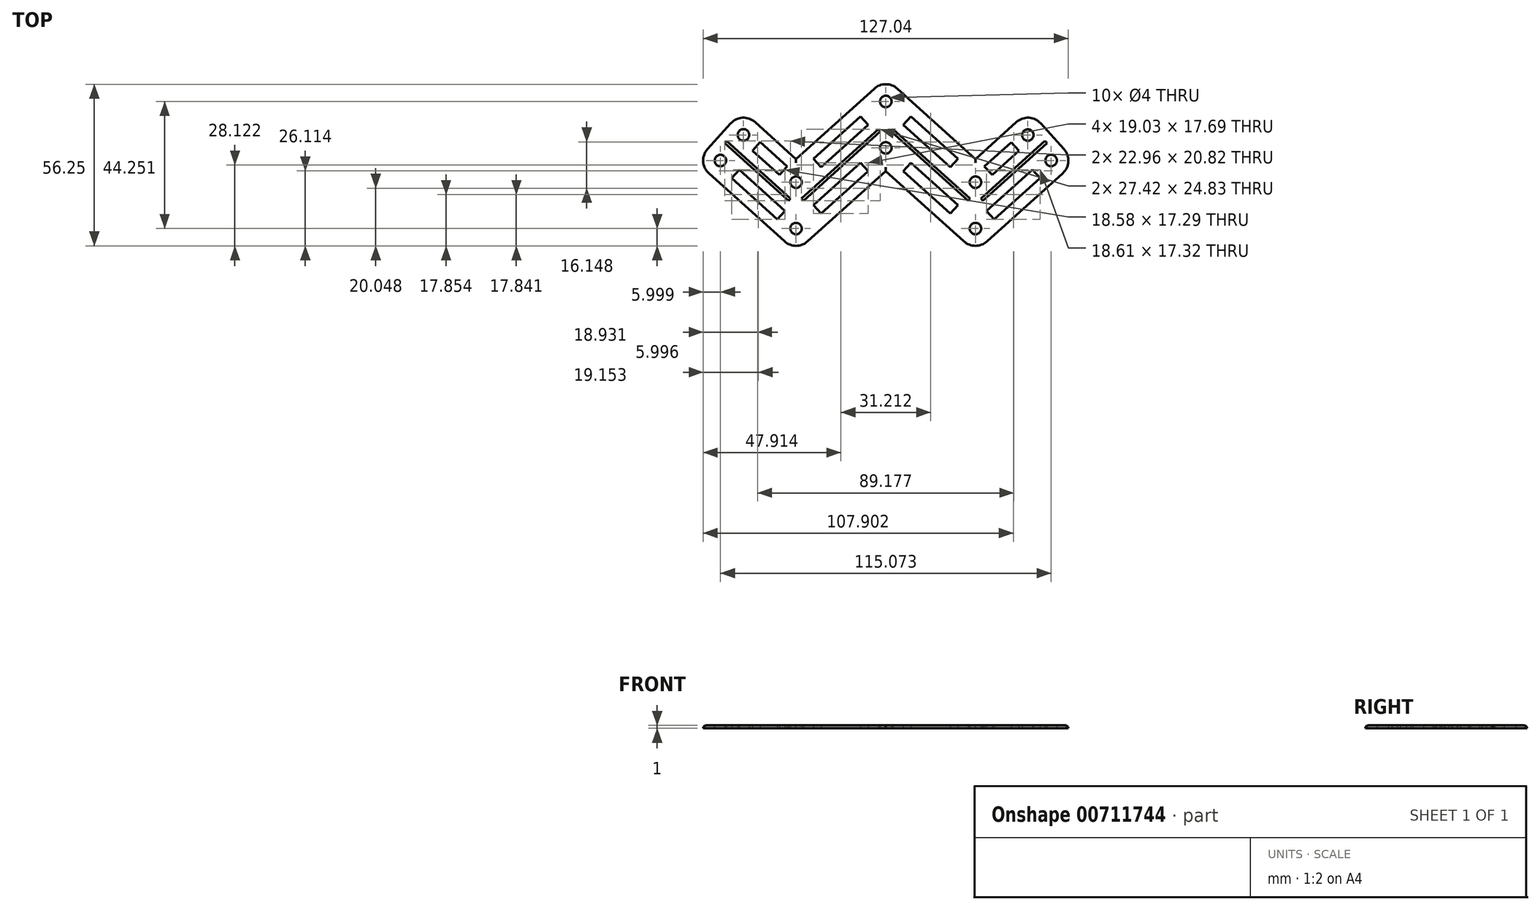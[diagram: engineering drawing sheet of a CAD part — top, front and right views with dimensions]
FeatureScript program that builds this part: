
annotation { "Feature Type Name" : "Feature", "Feature Type Description" : "" }
export const myFeature = defineFeature(function(context is Context, id is Id, definition is map)
    precondition{}
    {
        {
            var Q0;
            Q0=qCreatedBy(makeId("Top.planeOp"),FACE);
            var sketch = newSketch(context, id + "F0", { "sketchPlane" : qUnion([Q0])});
            skLineSegment(sketch, "E0", {"start": v(-57.97, 24.09) * mm, "end": v(-31.21, 0) * mm});
            skLineSegment(sketch, "E1", {"start": v(-31.21, 0) * mm, "end": v(0, 28.1) * mm});
            skLineSegment(sketch, "E2", {"start": v(0, 28.1) * mm, "end": v(31.21, 0) * mm});
            skLineSegment(sketch, "E3", {"start": v(31.21, 0) * mm, "end": v(57.97, 24.09) * mm});
            skLineSegment(sketch, "E4.0", {"start": v(31.21, -0.67) * mm, "end": v(58.3, 23.72) * mm});
            skLineSegment(sketch, "E4.1", {"start": v(0, 27.43) * mm, "end": v(31.21, -0.67) * mm});
            skLineSegment(sketch, "E4.2", {"start": v(-31.21, -0.67) * mm, "end": v(0, 27.43) * mm});
            skLineSegment(sketch, "E4.3", {"start": v(-58.3, 23.72) * mm, "end": v(-31.21, -0.67) * mm});
            skLineSegment(sketch, "E5.0", {"start": v(31.21, 0.67) * mm, "end": v(57.63, 24.46) * mm});
            skLineSegment(sketch, "E5.1", {"start": v(0, 28.78) * mm, "end": v(31.21, 0.67) * mm});
            skLineSegment(sketch, "E5.2", {"start": v(-31.21, 0.67) * mm, "end": v(0, 28.78) * mm});
            skLineSegment(sketch, "E5.3", {"start": v(-57.63, 24.46) * mm, "end": v(-31.21, 0.67) * mm});
            skLineSegment(sketch, "E6", {"start": v(-58.3, 23.72) * mm, "end": v(-57.97, 24.09) * mm});
            skLineSegment(sketch, "E7", {"start": v(-57.97, 24.09) * mm, "end": v(-57.63, 24.46) * mm});
            skLineSegment(sketch, "E8", {"start": v(57.63, 24.46) * mm, "end": v(57.97, 24.09) * mm});
            skLineSegment(sketch, "E9", {"start": v(58.3, 23.72) * mm, "end": v(57.97, 24.09) * mm});
            skLineSegment(sketch, "E10.0", {"start": v(35.23, -12.53) * mm, "end": v(61.54, 11.16) * mm});
            skLineSegment(sketch, "E10.1", {"start": v(0, 11.96) * mm, "end": v(27.2, -12.53) * mm});
            skLineSegment(sketch, "E10.2", {"start": v(-27.2, -12.53) * mm, "end": v(0, 11.96) * mm});
            skLineSegment(sketch, "E10.3", {"start": v(-61.54, 11.16) * mm, "end": v(-35.23, -12.53) * mm});
            skLineSegment(sketch, "E11.0", {"start": v(31.21, 16.15) * mm, "end": v(45.48, 29) * mm});
            skLineSegment(sketch, "E11.1", {"start": v(4.01, 40.64) * mm, "end": v(31.21, 16.15) * mm});
            skLineSegment(sketch, "E11.2", {"start": v(-31.21, 16.15) * mm, "end": v(-4.01, 40.64) * mm});
            skLineSegment(sketch, "E11.3", {"start": v(-45.48, 29) * mm, "end": v(-31.21, 16.15) * mm});
            skLineSegment(sketch, "E12", {"start": v(-61.98, 19.63) * mm, "end": v(-58.3, 23.72) * mm});
            skLineSegment(sketch, "E13", {"start": v(-53.95, 28.55) * mm, "end": v(-57.63, 24.46) * mm});
            skLineSegment(sketch, "E14", {"start": v(61.98, 19.63) * mm, "end": v(58.3, 23.72) * mm});
            skLineSegment(sketch, "E15", {"start": v(53.95, 28.55) * mm, "end": v(57.63, 24.46) * mm});
            skLineSegment(sketch, "E16.0", {"start": v(31.21, -8.07) * mm, "end": v(62.01, 19.66) * mm, "construction": true});
            skLineSegment(sketch, "E16.1", {"start": v(0, 20.03) * mm, "end": v(31.21, -8.07) * mm, "construction": true});
            skLineSegment(sketch, "E16.2", {"start": v(-31.21, -8.07) * mm, "end": v(0, 20.03) * mm, "construction": true});
            skLineSegment(sketch, "E16.3", {"start": v(-61.98, 19.63) * mm, "end": v(-31.21, -8.07) * mm, "construction": true});
            skLineSegment(sketch, "E17.0", {"start": v(31.21, 8.07) * mm, "end": v(53.9, 28.5) * mm, "construction": true});
            skLineSegment(sketch, "E17.1", {"start": v(0, 36.18) * mm, "end": v(31.21, 8.07) * mm, "construction": true});
            skLineSegment(sketch, "E17.2", {"start": v(-31.21, 8.07) * mm, "end": v(0, 36.18) * mm, "construction": true});
            skLineSegment(sketch, "E17.3", {"start": v(-53.95, 28.55) * mm, "end": v(-31.21, 8.07) * mm, "construction": true});
            skCircle(sketch, "E18", {"center": v(-31.21, 8.07) * mm, "radius": 2 * mm});
            skCircle(sketch, "E19", {"center": v(-31.21, -8.07) * mm, "radius": 2 * mm});
            skCircle(sketch, "E20", {"center": v(0, 20.03) * mm, "radius": 2 * mm});
            skCircle(sketch, "E21", {"center": v(0, 36.18) * mm, "radius": 2 * mm});
            skCircle(sketch, "E22", {"center": v(31.21, 8.07) * mm, "radius": 2 * mm});
            skCircle(sketch, "E23", {"center": v(31.21, -8.07) * mm, "radius": 2 * mm});
            skCircle(sketch, "E24", {"center": v(49.43, 24.48) * mm, "radius": 2 * mm});
            skCircle(sketch, "E25", {"center": v(57.55, 15.64) * mm, "radius": 2 * mm});
            skCircle(sketch, "E26", {"center": v(-57.52, 15.62) * mm, "radius": 2 * mm});
            skCircle(sketch, "E27", {"center": v(-49.5, 24.53) * mm, "radius": 2 * mm});
            skLineSegment(sketch, "E28.0", {"start": v(31.21, -10.77) * mm, "end": v(63.32, 18.14) * mm, "construction": true});
            skLineSegment(sketch, "E28.1", {"start": v(0, 17.34) * mm, "end": v(31.21, -10.77) * mm, "construction": true});
            skLineSegment(sketch, "E28.2", {"start": v(-31.21, -10.77) * mm, "end": v(0, 17.34) * mm, "construction": true});
            skLineSegment(sketch, "E28.3", {"start": v(-63.32, 18.14) * mm, "end": v(-31.21, -10.77) * mm, "construction": true});
            skLineSegment(sketch, "E29.0", {"start": v(31.21, -5.38) * mm, "end": v(60.64, 21.12) * mm, "construction": true});
            skLineSegment(sketch, "E29.1", {"start": v(4.01, 19.1) * mm, "end": v(31.21, -5.38) * mm, "construction": true});
            skLineSegment(sketch, "E29.2", {"start": v(-31.21, -5.38) * mm, "end": v(-4.01, 19.1) * mm, "construction": true});
            skLineSegment(sketch, "E29.3", {"start": v(-60.64, 21.12) * mm, "end": v(-31.21, -5.38) * mm, "construction": true});
            skLineSegment(sketch, "E30.0", {"start": v(31.21, 10.77) * mm, "end": v(52.61, 30.03) * mm, "construction": true});
            skLineSegment(sketch, "E30.1", {"start": v(0, 38.87) * mm, "end": v(31.21, 10.77) * mm, "construction": true});
            skLineSegment(sketch, "E30.2", {"start": v(-31.21, 10.77) * mm, "end": v(0, 38.87) * mm, "construction": true});
            skLineSegment(sketch, "E30.3", {"start": v(-52.61, 30.03) * mm, "end": v(-31.21, 10.77) * mm, "construction": true});
            skLineSegment(sketch, "E31.0", {"start": v(31.21, 5.38) * mm, "end": v(55.29, 27.06) * mm, "construction": true});
            skLineSegment(sketch, "E31.1", {"start": v(0, 33.49) * mm, "end": v(31.21, 5.38) * mm, "construction": true});
            skLineSegment(sketch, "E31.2", {"start": v(-31.21, 5.38) * mm, "end": v(0, 33.49) * mm, "construction": true});
            skLineSegment(sketch, "E31.3", {"start": v(-55.29, 27.06) * mm, "end": v(-31.21, 5.38) * mm, "construction": true});
            skLineSegment(sketch, "E32", {"start": v(-25.12, 16.25) * mm, "end": v(-8.77, 30.97) * mm});
            skLineSegment(sketch, "E33", {"start": v(-8.77, 30.97) * mm, "end": v(-6.1, 28) * mm});
            skLineSegment(sketch, "E34", {"start": v(-25.12, 16.25) * mm, "end": v(-22.44, 13.28) * mm});
            skLineSegment(sketch, "E35", {"start": v(-22.44, 13.28) * mm, "end": v(-6.1, 28) * mm});
            skLineSegment(sketch, "E36", {"start": v(-43.7, 22) * mm, "end": v(-46.37, 19.03) * mm});
            skLineSegment(sketch, "E37", {"start": v(-46.37, 19.03) * mm, "end": v(-37.03, 10.62) * mm});
            skLineSegment(sketch, "E38", {"start": v(-37.03, 10.62) * mm, "end": v(-34.31, 13.56) * mm});
            skLineSegment(sketch, "E39", {"start": v(-34.31, 13.56) * mm, "end": v(-43.7, 22) * mm});
            skLineSegment(sketch, "E40", {"start": v(-50.98, 12.42) * mm, "end": v(-53.66, 9.44) * mm});
            skLineSegment(sketch, "E41", {"start": v(-53.66, 9.44) * mm, "end": v(-37.75, -4.88) * mm});
            skLineSegment(sketch, "E42", {"start": v(-37.75, -4.88) * mm, "end": v(-35.08, -1.9) * mm});
            skLineSegment(sketch, "E43", {"start": v(-35.08, -1.9) * mm, "end": v(-50.98, 12.42) * mm});
            skLineSegment(sketch, "E44", {"start": v(-22.44, -2.87) * mm, "end": v(-25.12, 0.1) * mm});
            skLineSegment(sketch, "E45", {"start": v(-25.12, 0.1) * mm, "end": v(-8.77, 14.82) * mm});
            skLineSegment(sketch, "E46", {"start": v(-8.77, 14.82) * mm, "end": v(-6.1, 11.85) * mm});
            skLineSegment(sketch, "E47", {"start": v(-6.1, 11.85) * mm, "end": v(-22.44, -2.87) * mm});
            skLineSegment(sketch, "E48", {"start": v(8.77, 30.97) * mm, "end": v(6.1, 28) * mm});
            skLineSegment(sketch, "E49", {"start": v(6.1, 28) * mm, "end": v(22.44, 13.28) * mm});
            skLineSegment(sketch, "E50", {"start": v(22.44, 13.28) * mm, "end": v(25.12, 16.25) * mm});
            skLineSegment(sketch, "E51", {"start": v(25.12, 16.25) * mm, "end": v(8.77, 30.97) * mm});
            skLineSegment(sketch, "E52", {"start": v(6.1, 11.85) * mm, "end": v(8.77, 14.82) * mm});
            skLineSegment(sketch, "E53", {"start": v(8.77, 14.82) * mm, "end": v(25.12, 0.1) * mm});
            skLineSegment(sketch, "E54", {"start": v(25.12, 0.1) * mm, "end": v(22.44, -2.87) * mm});
            skLineSegment(sketch, "E55", {"start": v(22.44, -2.87) * mm, "end": v(6.1, 11.85) * mm});
            skLineSegment(sketch, "E56", {"start": v(34.33, 13.57) * mm, "end": v(37, 10.6) * mm});
            skLineSegment(sketch, "E57", {"start": v(37, 10.6) * mm, "end": v(46.31, 18.98) * mm});
            skLineSegment(sketch, "E58", {"start": v(46.31, 18.98) * mm, "end": v(43.64, 21.95) * mm});
            skLineSegment(sketch, "E59", {"start": v(43.64, 21.95) * mm, "end": v(34.33, 13.57) * mm});
            skLineSegment(sketch, "E60", {"start": v(35.08, -1.9) * mm, "end": v(37.75, -4.88) * mm});
            skLineSegment(sketch, "E61", {"start": v(37.75, -4.88) * mm, "end": v(53.69, 9.47) * mm});
            skLineSegment(sketch, "E62", {"start": v(53.69, 9.47) * mm, "end": v(51.01, 12.44) * mm});
            skLineSegment(sketch, "E63", {"start": v(51.01, 12.44) * mm, "end": v(35.08, -1.9) * mm});
            skPoint(sketch, "E64.visualSharp", {"position": v(-49.94, 33) * mm});
            skArc(sketch, "E64.filletArc", {"start": v(-45.48, 29) * mm, "mid": v(-49.8, 30.52) * mm, "end": v(-53.95, 28.55) * mm});
            skPoint(sketch, "E65.visualSharp", {"position": v(-66, 15.17) * mm});
            skArc(sketch, "E65.filletArc", {"start": v(-61.98, 19.63) * mm, "mid": v(-63.51, 15.3) * mm, "end": v(-61.54, 11.16) * mm});
            skPoint(sketch, "E66.visualSharp", {"position": v(-31.21, -16.15) * mm});
            skArc(sketch, "E66.filletArc", {"start": v(-35.23, -12.53) * mm, "mid": v(-31.21, -14.07) * mm, "end": v(-27.2, -12.53) * mm});
            skPoint(sketch, "E67.visualSharp", {"position": v(0, 22.72) * mm});
            skArc(sketch, "E67.filletArc", {"start": v(4.01, 19.1) * mm, "mid": v(0, 20.65) * mm, "end": v(-4.01, 19.1) * mm, "construction": true});
            skPoint(sketch, "E68.visualSharp", {"position": v(0, 44.25) * mm});
            skArc(sketch, "E68.filletArc", {"start": v(4.01, 40.64) * mm, "mid": v(0, 42.18) * mm, "end": v(-4.01, 40.64) * mm});
            skPoint(sketch, "E69.visualSharp", {"position": v(31.21, -16.15) * mm});
            skArc(sketch, "E69.filletArc", {"start": v(27.2, -12.53) * mm, "mid": v(31.21, -14.07) * mm, "end": v(35.23, -12.53) * mm});
            skPoint(sketch, "E70.visualSharp", {"position": v(66, 15.17) * mm});
            skArc(sketch, "E70.filletArc", {"start": v(61.54, 11.16) * mm, "mid": v(63.51, 15.3) * mm, "end": v(61.98, 19.63) * mm});
            skPoint(sketch, "E71.visualSharp", {"position": v(49.94, 33) * mm});
            skArc(sketch, "E71.filletArc", {"start": v(53.95, 28.55) * mm, "mid": v(49.8, 30.52) * mm, "end": v(45.48, 29) * mm});
            skLineSegment(sketch, "E72", {"start": v(33.78, 1.64) * mm, "end": v(33.1, 2.38) * mm});
            skLineSegment(sketch, "E73", {"start": v(33.1, 2.38) * mm, "end": v(55.4, 22.45) * mm});
            skLineSegment(sketch, "E74", {"start": v(55.4, 22.45) * mm, "end": v(56.07, 21.7) * mm});
            skLineSegment(sketch, "E75", {"start": v(56.07, 21.7) * mm, "end": v(33.78, 1.64) * mm});
            skLineSegment(sketch, "E76", {"start": v(28.65, 1.64) * mm, "end": v(29.32, 2.38) * mm});
            skLineSegment(sketch, "E77", {"start": v(29.32, 2.38) * mm, "end": v(2.56, 26.47) * mm});
            skLineSegment(sketch, "E78", {"start": v(2.56, 26.47) * mm, "end": v(1.9, 25.72) * mm});
            skLineSegment(sketch, "E79", {"start": v(1.9, 25.72) * mm, "end": v(28.65, 1.64) * mm});
            skLineSegment(sketch, "E80", {"start": v(-2.56, 26.47) * mm, "end": v(-1.9, 25.72) * mm});
            skLineSegment(sketch, "E81", {"start": v(-1.9, 25.72) * mm, "end": v(-28.65, 1.64) * mm});
            skLineSegment(sketch, "E82", {"start": v(-28.65, 1.64) * mm, "end": v(-29.32, 2.38) * mm});
            skLineSegment(sketch, "E83", {"start": v(-29.32, 2.38) * mm, "end": v(-2.56, 26.47) * mm});
            skLineSegment(sketch, "E84", {"start": v(-33.78, 1.64) * mm, "end": v(-33.1, 2.38) * mm});
            skLineSegment(sketch, "E85", {"start": v(-33.1, 2.38) * mm, "end": v(-55.4, 22.45) * mm});
            skLineSegment(sketch, "E86", {"start": v(-55.4, 22.45) * mm, "end": v(-56.07, 21.7) * mm});
            skLineSegment(sketch, "E87", {"start": v(-56.07, 21.7) * mm, "end": v(-33.78, 1.64) * mm});
            skSolve(sketch);
        }
        {
            var Q0;
            Q0=makeQuery(id+"F0.imprint","IMPRINT",FACE,{"disambiguationData":[TD([[makeQuery(id+"F0.imprint","IMPRINT",EDGE,{"derivedFrom":sQuery(id+"F0.wireOp",EDGE,"E10.0")}),1.0]])]});
            var Q1;
            {var subQ0=sQuery(id+"F0.wireOp",EDGE,"E6");Q1=makeQuery(id+"F0.imprint","IMPRINT",FACE,{"disambiguationData":[TD([[makeQuery(id+"F0.imprint","IMPRINT",EDGE,{"derivedFrom":subQ0}),-1.0]])]});}
            var Q2;
            {var subQ0=sQuery(id+"F0.wireOp",EDGE,"E7");Q2=makeQuery(id+"F0.imprint","IMPRINT",FACE,{"disambiguationData":[TD([[makeQuery(id+"F0.imprint","IMPRINT",EDGE,{"derivedFrom":subQ0}),-1.0]])]});}
            var Q3;
            Q3=makeQuery(id+"F0.imprint","IMPRINT",FACE,{"disambiguationData":[TD([[makeQuery(id+"F0.imprint","IMPRINT",EDGE,{"derivedFrom":sQuery(id+"F0.wireOp",EDGE,"E11.0")}),-1.0]])]});
            var Q4;
            {var subQ7=sQuery(id+"F0.wireOp",EDGE,"E1");var subQ8=sQuery(id+"F0.wireOp",EDGE,"E0");var subQ9=makeQuery(id+"F0.imprint","INTERSECT",VERTEX,{"derivedFrom":[subQ8,subQ7]});Q4=makeQuery(id+"F0.imprint","IMPRINT",FACE,{"disambiguationData":[TD([[makeQuery(id+"F0.imprint","IMPRINT",EDGE,{"disambiguationData":[TD([[subQ9,1.0]])],"derivedFrom":subQ8}),-1.0]])]});}
            var Q5;
            {var subQ5=sQuery(id+"F0.wireOp",EDGE,"E1");var subQ6=sQuery(id+"F0.wireOp",EDGE,"E0");var subQ7=makeQuery(id+"F0.imprint","INTERSECT",VERTEX,{"derivedFrom":[subQ6,subQ5]});Q5=makeQuery(id+"F0.imprint","IMPRINT",FACE,{"disambiguationData":[TD([[makeQuery(id+"F0.imprint","IMPRINT",EDGE,{"disambiguationData":[TD([[subQ7,1.0]])],"derivedFrom":subQ6}),1.0]])]});}
            var Q6;
            {var subQ5=sQuery(id+"F0.wireOp",EDGE,"E2");var subQ6=sQuery(id+"F0.wireOp",EDGE,"E1");var subQ7=makeQuery(id+"F0.imprint","INTERSECT",VERTEX,{"derivedFrom":[subQ6,subQ5]});Q6=makeQuery(id+"F0.imprint","IMPRINT",FACE,{"disambiguationData":[TD([[makeQuery(id+"F0.imprint","IMPRINT",EDGE,{"disambiguationData":[TD([[subQ7,1.0]])],"derivedFrom":subQ6}),-1.0]])]});}
            var Q7;
            {var subQ5=sQuery(id+"F0.wireOp",EDGE,"E2");var subQ6=sQuery(id+"F0.wireOp",EDGE,"E1");var subQ7=makeQuery(id+"F0.imprint","INTERSECT",VERTEX,{"derivedFrom":[subQ6,subQ5]});Q7=makeQuery(id+"F0.imprint","IMPRINT",FACE,{"disambiguationData":[TD([[makeQuery(id+"F0.imprint","IMPRINT",EDGE,{"disambiguationData":[TD([[subQ7,1.0]])],"derivedFrom":subQ6}),1.0]])]});}
            var Q8;
            {var subQ7=sQuery(id+"F0.wireOp",EDGE,"E3");var subQ8=sQuery(id+"F0.wireOp",EDGE,"E2");var subQ9=makeQuery(id+"F0.imprint","INTERSECT",VERTEX,{"derivedFrom":[subQ8,subQ7]});Q8=makeQuery(id+"F0.imprint","IMPRINT",FACE,{"disambiguationData":[TD([[makeQuery(id+"F0.imprint","IMPRINT",EDGE,{"disambiguationData":[TD([[subQ9,1.0]])],"derivedFrom":subQ8}),-1.0]])]});}
            var Q9;
            {var subQ5=sQuery(id+"F0.wireOp",EDGE,"E3");var subQ6=sQuery(id+"F0.wireOp",EDGE,"E2");var subQ7=makeQuery(id+"F0.imprint","INTERSECT",VERTEX,{"derivedFrom":[subQ6,subQ5]});Q9=makeQuery(id+"F0.imprint","IMPRINT",FACE,{"disambiguationData":[TD([[makeQuery(id+"F0.imprint","IMPRINT",EDGE,{"disambiguationData":[TD([[subQ7,1.0]])],"derivedFrom":subQ6}),1.0]])]});}
            var Q10;
            {var subQ0=sQuery(id+"F0.wireOp",EDGE,"E9");Q10=makeQuery(id+"F0.imprint","IMPRINT",FACE,{"disambiguationData":[TD([[makeQuery(id+"F0.imprint","IMPRINT",EDGE,{"derivedFrom":subQ0}),1.0]])]});}
            var Q11;
            {var subQ0=sQuery(id+"F0.wireOp",EDGE,"E8");Q11=makeQuery(id+"F0.imprint","IMPRINT",FACE,{"disambiguationData":[TD([[makeQuery(id+"F0.imprint","IMPRINT",EDGE,{"derivedFrom":subQ0}),-1.0]])]});}
            extrude(context, id + "F1", {"entities" : qUnion([Q0, Q1, Q2, Q3, Q4, Q5, Q6, Q7, Q8, Q9, Q10, Q11]), "flatOperationType" : FlatOperationType.REMOVE, "depth" : 1 * mm, "offsetDistance" : 25 * mm, "domain" : OperationDomain.MODEL});
        }
        {
            var Q0;
            Q0=makeQuery(id+"F1.opExtrude","CAP_EDGE",EDGE,{"disambiguationData":[OSD([sQuery(id+"F0.wireOp",EDGE,"E65.filletArc")])],"isStart":false});
            var Q1;
            Q1=makeQuery(id+"F1.opExtrude","CAP_EDGE",EDGE,{"disambiguationData":[OSD([sQuery(id+"F0.wireOp",EDGE,"E10.3")])],"isStart":false});
            var Q2;
            Q2=makeQuery(id+"F1.opExtrude","CAP_EDGE",EDGE,{"disambiguationData":[OSD([sQuery(id+"F0.wireOp",EDGE,"E66.filletArc")])],"isStart":false});
            var Q3;
            Q3=makeQuery(id+"F1.opExtrude","CAP_EDGE",EDGE,{"disambiguationData":[OSD([sQuery(id+"F0.wireOp",EDGE,"E10.2")])],"isStart":false});
            var Q4;
            Q4=makeQuery(id+"F1.opExtrude","CAP_EDGE",EDGE,{"disambiguationData":[OSD([sQuery(id+"F0.wireOp",EDGE,"E10.1")])],"isStart":false});
            var Q5;
            Q5=makeQuery(id+"F1.opExtrude","CAP_EDGE",EDGE,{"disambiguationData":[OSD([sQuery(id+"F0.wireOp",EDGE,"E69.filletArc")])],"isStart":false});
            var Q6;
            Q6=makeQuery(id+"F1.opExtrude","CAP_EDGE",EDGE,{"disambiguationData":[OSD([sQuery(id+"F0.wireOp",EDGE,"E10.0")])],"isStart":false});
            var Q7;
            Q7=makeQuery(id+"F1.opExtrude","CAP_EDGE",EDGE,{"disambiguationData":[OSD([sQuery(id+"F0.wireOp",EDGE,"E70.filletArc")])],"isStart":false});
            var Q8;
            Q8=makeQuery(id+"F1.opExtrude","CAP_EDGE",EDGE,{"disambiguationData":[OSD([sQuery(id+"F0.wireOp",EDGE,"E8"),sQuery(id+"F0.wireOp",EDGE,"E9"),sQuery(id+"F0.wireOp",EDGE,"E14"),sQuery(id+"F0.wireOp",EDGE,"E15")])],"isStart":false});
            var Q9;
            Q9=makeQuery(id+"F1.opExtrude","CAP_EDGE",EDGE,{"disambiguationData":[OSD([sQuery(id+"F0.wireOp",EDGE,"E71.filletArc")])],"isStart":false});
            var Q10;
            Q10=makeQuery(id+"F1.opExtrude","CAP_EDGE",EDGE,{"disambiguationData":[OSD([sQuery(id+"F0.wireOp",EDGE,"E11.0")])],"isStart":false});
            var Q11;
            Q11=makeQuery(id+"F1.opExtrude","CAP_EDGE",EDGE,{"disambiguationData":[OSD([sQuery(id+"F0.wireOp",EDGE,"E11.1")])],"isStart":false});
            var Q12;
            Q12=makeQuery(id+"F1.opExtrude","CAP_EDGE",EDGE,{"disambiguationData":[OSD([sQuery(id+"F0.wireOp",EDGE,"E68.filletArc")])],"isStart":false});
            var Q13;
            Q13=makeQuery(id+"F1.opExtrude","CAP_EDGE",EDGE,{"disambiguationData":[OSD([sQuery(id+"F0.wireOp",EDGE,"E11.2")])],"isStart":false});
            var Q14;
            Q14=makeQuery(id+"F1.opExtrude","CAP_EDGE",EDGE,{"disambiguationData":[OSD([sQuery(id+"F0.wireOp",EDGE,"E11.3")])],"isStart":false});
            var Q15;
            Q15=makeQuery(id+"F1.opExtrude","CAP_EDGE",EDGE,{"disambiguationData":[OSD([sQuery(id+"F0.wireOp",EDGE,"E64.filletArc")])],"isStart":false});
            var Q16;
            Q16=makeQuery(id+"F1.opExtrude","CAP_EDGE",EDGE,{"disambiguationData":[OSD([sQuery(id+"F0.wireOp",EDGE,"E6"),sQuery(id+"F0.wireOp",EDGE,"E7"),sQuery(id+"F0.wireOp",EDGE,"E12"),sQuery(id+"F0.wireOp",EDGE,"E13")])],"isStart":false});
            fillet(context, id + "F2", {"entities" : qUnion([Q0, Q1, Q2, Q3, Q4, Q5, Q6, Q7, Q8, Q9, Q10, Q11, Q12, Q13, Q14, Q15, Q16]), "radius" : 1 * mm, "tangentPropagation" : true, "allowEdgeOverflow" : false});
        }
    });
